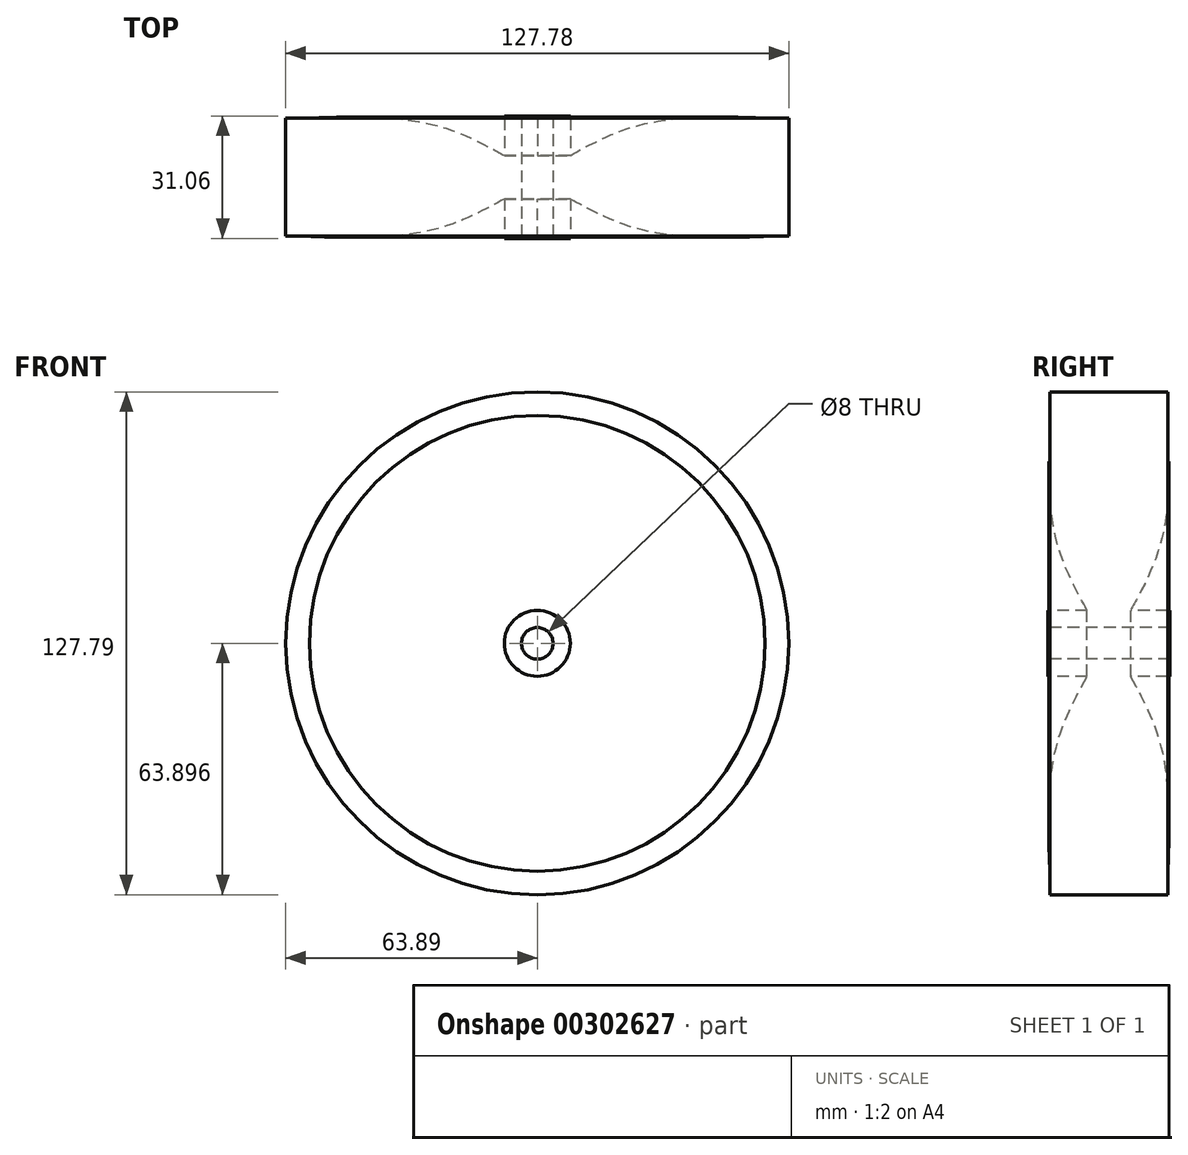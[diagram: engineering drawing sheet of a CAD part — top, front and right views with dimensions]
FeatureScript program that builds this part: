
annotation { "Feature Type Name" : "Feature", "Feature Type Description" : "" }
export const myFeature = defineFeature(function(context is Context, id is Id, definition is map)
    precondition{}
    {
        {
            var Q0;
            Q0=qCreatedBy(makeId("Right.planeOp"),FACE);
            var sketch = newSketch(context, id + "F0", { "sketchPlane" : qUnion([Q0])});
            skCircle(sketch, "E0", {"center": v(0, 0) * mm, "radius": 76.69 * mm});
            skLineSegment(sketch, "E1.bottom", {"start": v(-15, 75.2) * mm, "end": v(15, 75.2) * mm});
            skLineSegment(sketch, "E1.top", {"start": v(-15, 69.2) * mm, "end": v(15, 69.2) * mm});
            skLineSegment(sketch, "E1.left", {"start": v(-15, 75.2) * mm, "end": v(-15, 69.2) * mm});
            skLineSegment(sketch, "E1.right", {"start": v(15, 75.2) * mm, "end": v(15, 69.2) * mm});
            skFitSpline(sketch, "E2", {"points": [v(-15, 69.2) * mm, v(-5.53, 19.7) * mm], "startDerivative": vector(-3.28, -82.5) * mm, "endDerivative": vector(25.4, -45.7) * mm});
            skLineSegment(sketch, "E3", {"start": v(-5.53, 19.7) * mm, "end": v(-15.53, 19.7) * mm});
            skLineSegment(sketch, "E4", {"start": v(-15.53, 19.7) * mm, "end": v(-15.53, 15.32) * mm});
            skLineSegment(sketch, "E5", {"start": v(-15.53, 15.32) * mm, "end": v(5.57, 15.32) * mm});
            skFitSpline(sketch, "E6.MirrorCS", {"points": [v(15, 69.2) * mm, v(5.53, 19.7) * mm], "startDerivative": vector(3.28, -82.5) * mm, "endDerivative": vector(-25.4, -45.7) * mm});
            skLineSegment(sketch, "E7.MirrorCS", {"start": v(5.53, 19.7) * mm, "end": v(15.53, 19.7) * mm});
            skLineSegment(sketch, "E8.MirrorCS", {"start": v(15.53, 19.7) * mm, "end": v(15.53, 15.32) * mm});
            skLineSegment(sketch, "E9.MirrorCS", {"start": v(15.53, 15.32) * mm, "end": v(-5.57, 15.32) * mm});
            skLineSegment(sketch, "E10", {"start": v(-52.55, 11.32) * mm, "end": v(84.56, 11.32) * mm});
            skSolve(sketch);
        }
        {
            var Q0;
            Q0=makeQuery(id+"F0.imprint","IMPRINT",FACE,{"disambiguationData":[TD([[makeQuery(id+"F0.imprint","IMPRINT",EDGE,{"derivedFrom":sQuery(id+"F0.wireOp",EDGE,"E1.bottom")}),-1.0]])]});
            var Q1;
            Q1=makeQuery(id+"F0.imprint","IMPRINT",FACE,{"disambiguationData":[TD([[makeQuery(id+"F0.imprint","IMPRINT",EDGE,{"derivedFrom":sQuery(id+"F0.wireOp",EDGE,"E1.top")}),-1.0]])]});
            var Q2;
            Q2=sQuery(id+"F0.wireOp",EDGE,"E10");
            revolve(context, id + "F1", {"entities" : qUnion([Q0, Q1]), "axis" : qUnion([Q2]), "revolveType" : RevolveType.FULL});
        }
    });
